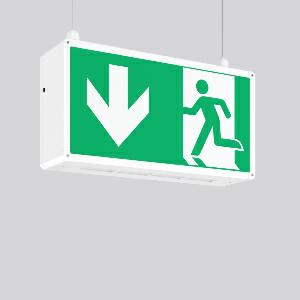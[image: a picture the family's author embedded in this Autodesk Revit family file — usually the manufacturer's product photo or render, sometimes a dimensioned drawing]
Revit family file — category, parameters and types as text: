
# Revit family: rechteck_seilpendel_671351_002_83ce
name_source: partatom
category: Lighting Fixtures
units: mm (PartAtom-declared; Revit-internal decimal feet)

## family parameters
Cut with Voids When Loaded = No
Host = Face
Light Source = No
Part Type = Normal
Room Calculation Point = No
Round Connector Dimension = Use Diameter
Shared = No

## types (1)
- RECHTECK seilpendel
    Apparent Load = 0 VA
    Default Elevation = 1800 mm
    Description = Series: RECHTECK
Rectangular pendant luminaire in classic design. For escape route identification. Housing: aluminium, with plastic corner connectors. Display panels: plastic, opal, with motifs on one side/on both sides. Pendant luminaires (suspension provided on site) ready for connection to two suspension cables or chains. Electronic ballast included. Self-contained system with automatic self-test. Please indicate legend number when placing your order! 
Colour: white
Length: 485 mm
Width: 125 mm
Height: 250 mm
Weight: 3.11 kg
Operating mode: maintained power mode
Viewing Distance: 43 m
Duration time: 3 h
Lamp: LED
Socket: without socket
Colour temperature: 6500K
Colour rendering index (CRI): 70
System power: 9.1 W
Control gear: Regulated power supply
Protection class: I
Type of protection: IP 44
    Height = 250 mm
    Lamp = 0 x
    Length = 485 mm
    Luminous efficacy = 0 lm/W
    Manufacturer = RZB
    ModVariant = No
    Model = 671351.002
    Mounting Place = Ceiling
    Mounting Type = Pendant
    Number of Poles = 1
    OnlyDefault = Yes
    Power Factor = 1
    Product Name = RECHTECK seilpendel
    Product group = Pendant luminaires
    ProductGroupID = 902
    Protection Class = Protection class I
    Protection Degree = IP 44
    RLX_Detail_Level = 1
    RLX_Emergency_Light_Flux = 0 lm
    RLX_Emergency_Type = 0
    RLX_Emergency_Type_DB = No
    RlxData = <blob elided: 56917 chars, md5=edd32cc7>
    Standby Power = 0 W
    System Light Flux = 0 lm
    System Power = 0 W
    Type Comments = Product without accessories
    Type Image = 671351.002.jpg
    URL = http://relux.com
    VarID = ---
    Voltage = 230 V
    Voltage Range = 220-240 V
    Weight = 0.00 kg
    Width = 125 mm

## geometry (parser evidence)
native form markers: Blend x4, Sweep x12
no freeform markers — native parametric forms only
